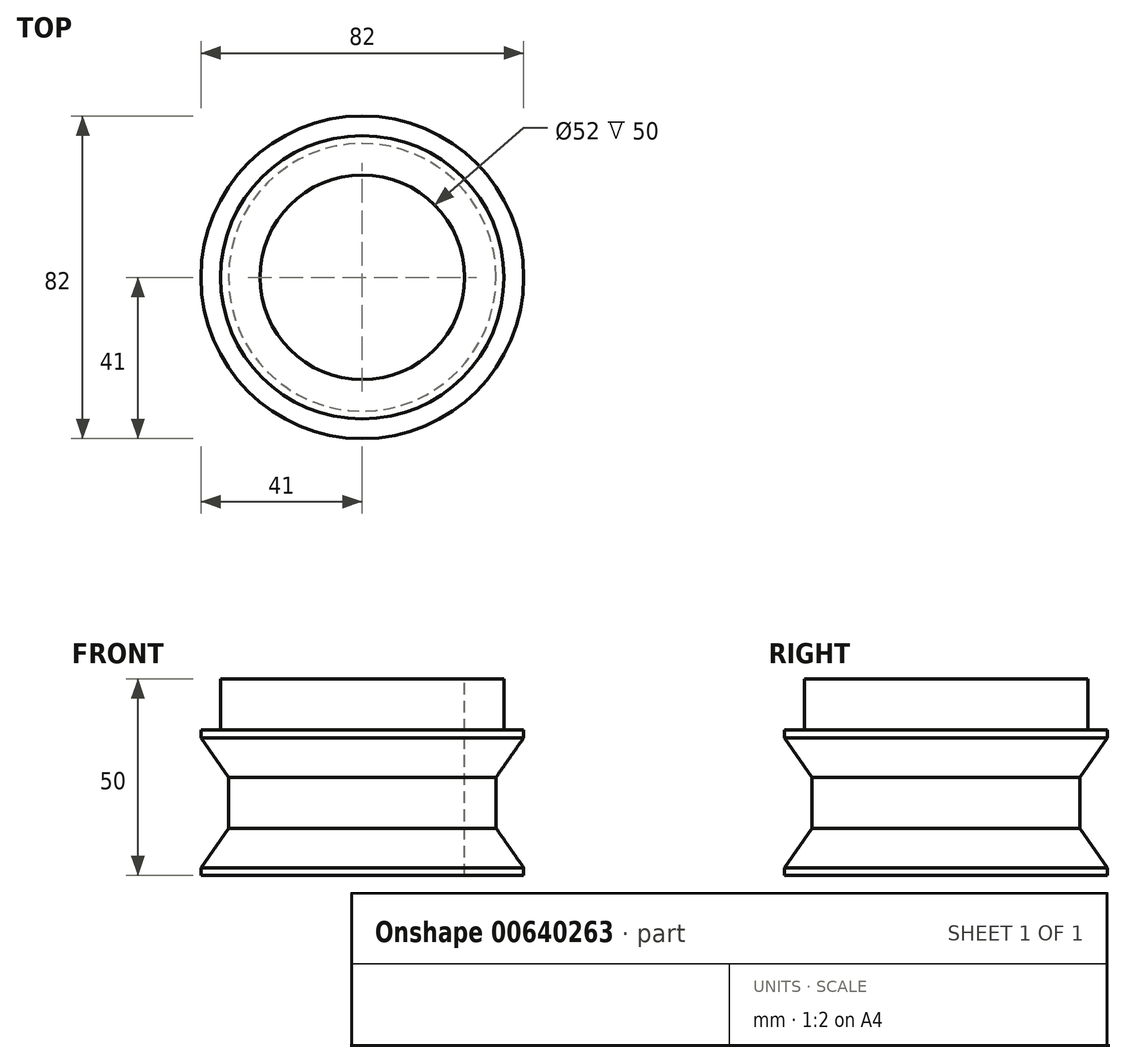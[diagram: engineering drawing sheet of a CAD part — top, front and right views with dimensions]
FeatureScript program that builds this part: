
annotation { "Feature Type Name" : "Feature", "Feature Type Description" : "" }
export const myFeature = defineFeature(function(context is Context, id is Id, definition is map)
    precondition{}
    {
        {
            var Q0;
            Q0=qCreatedBy(makeId("Front.planeOp"),FACE);
            var sketch = newSketch(context, id + "F0", { "sketchPlane" : qUnion([Q0])});
            skLineSegment(sketch, "E0", {"start": v(14.5, 0) * mm, "end": v(14.5, 2) * mm});
            skLineSegment(sketch, "E1", {"start": v(14.5, 2) * mm, "end": v(7.5, 12) * mm});
            skLineSegment(sketch, "E2", {"start": v(7.5, 12) * mm, "end": v(7.5, 25) * mm});
            skLineSegment(sketch, "E3", {"start": v(7.5, 25) * mm, "end": v(14.5, 35) * mm});
            skLineSegment(sketch, "E4", {"start": v(14.5, 35) * mm, "end": v(14.5, 37) * mm});
            skLineSegment(sketch, "E5", {"start": v(14.5, 37) * mm, "end": v(9.5, 37) * mm});
            skLineSegment(sketch, "E6", {"start": v(9.5, 37) * mm, "end": v(9.5, 50) * mm});
            skLineSegment(sketch, "E7", {"start": v(9.5, 50) * mm, "end": v(-0.5, 50) * mm});
            skLineSegment(sketch, "E8", {"start": v(-0.5, 50) * mm, "end": v(-0.5, 0) * mm});
            skLineSegment(sketch, "E9", {"start": v(-0.5, 0) * mm, "end": v(14.5, 0) * mm});
            skLineSegment(sketch, "E10", {"start": v(-26.5, 57.83) * mm, "end": v(-26.5, -11.48) * mm});
            skSolve(sketch);
        }
        {
            var Q0;
            Q0=makeQuery(id+"F0.imprint","IMPRINT",FACE,{"disambiguationData":[TD([[makeQuery(id+"F0.imprint","IMPRINT",EDGE,{"derivedFrom":sQuery(id+"F0.wireOp",EDGE,"E0")}),1.0]])]});
            var Q1;
            Q1=sQuery(id+"F0.wireOp",EDGE,"E2");
            var Q2;
            Q2=sQuery(id+"F0.wireOp",EDGE,"E5");
            var Q3;
            Q3=sQuery(id+"F0.wireOp",EDGE,"E3");
            var Q4;
            Q4=sQuery(id+"F0.wireOp",EDGE,"E1");
            var Q5;
            Q5=sQuery(id+"F0.wireOp",EDGE,"E6");
            var Q6;
            Q6=sQuery(id+"F0.wireOp",EDGE,"E7");
            var Q7;
            Q7=sQuery(id+"F0.wireOp",EDGE,"E8");
            var Q8;
            Q8=sQuery(id+"F0.wireOp",EDGE,"E9");
            var Q9;
            Q9=sQuery(id+"F0.wireOp",EDGE,"E4");
            var Q10;
            Q10=sQuery(id+"F0.wireOp",EDGE,"E0");
            var Q11;
            Q11=sQuery(id+"F0.wireOp",EDGE,"E10");
            revolve(context, id + "F1", {"entities" : qUnion([Q0]), "surfaceEntities" : qUnion([Q1, Q2, Q3, Q4, Q5, Q6, Q7, Q8, Q9, Q10]), "axis" : qUnion([Q11]), "revolveType" : RevolveType.FULL});
        }
    });
